# Revit family: Emergency_Equipment-Haws_Corporation-Shower_8770
name_source: partatom
category: Plumbing Fixtures
revit_build: Autodesk Revit 2018 (Build: 20170223_1515(x64)
units: mm (PartAtom-declared; Revit-internal decimal feet)

## family parameters
Always vertical = Yes
Cut with Voids When Loaded = No
OmniClass Number = 23.45.05.14.17
Part Type = Normal
Room Calculation Point = No
Round Connector Dimension = Use Diameter
Shared = No
Work Plane-Based = No

## types (1)
- 8770 - Indoor Gravity Fed Emergency Shower
    Assembly Code = D2010710
    Depth = 120"
    Description = Indoor Gravity Fed Emergency Shower
    Edition number = 1
    Finish = Metal - Haws Corporation - Green
    Flow = 20 GPM
    Height = 102"
    Keynote = 12500
    Manufacturer = Haws Corporation
    Model = 8770
    Number of Poles = 1
    Phase = 3
    Power Factor = 1
    Product Guid = 68226a8c-b434-4d8d-9c40-692a15fef11a
    Product data url = https://www.bimobject.com
    Sanitary Diameter = 2 3/4"
    Supply Diameter = 1 1/2"
    URL = https://www.hawsco.com
    Vent Connection = No
    Voltage = 480 V
    Width = 66"

## geometry (parser evidence)
native form markers: Sweep x4
no freeform markers — native parametric forms only
